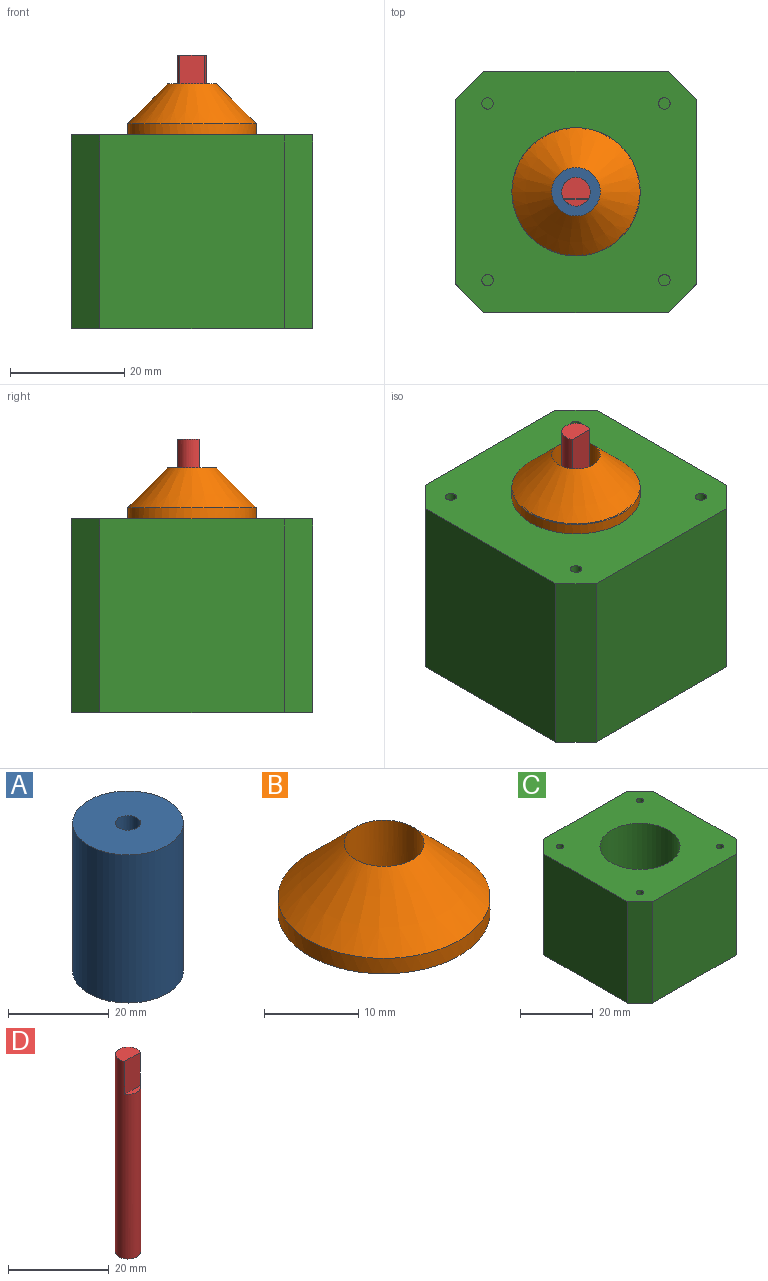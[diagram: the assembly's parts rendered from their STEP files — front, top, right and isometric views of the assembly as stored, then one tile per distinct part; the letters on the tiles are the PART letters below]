
ASSEMBLY  parts=4 mates=3
PART A: 4 faces, bbox 22x22x36 mm
  f0: cylinder r=2.5mm len=36mm, axis (0,0,-1), area 565.5mm2, adj f2,f3
  f1: cylinder r=11mm len=36mm, axis (0,0,-1), area 2488.1mm2, adj f2,f3
  f2: plane 22x22mm, normal (0,0,1), area 360.5mm2, adj f0,f1
  f3: plane 22x22mm, normal (0,0,-1), area 360.5mm2, adj f0,f1
PART B: 4 faces, bbox 22.5x22.5x9 mm
  f0: cylinder r=11.25mm len=22.5mm, axis (0,0,-1), area 141.4mm2, adj f2,f3
  f1: cylinder r=4.25mm len=9mm, axis (0,0,-1), area 240.3mm2, adj f2,f3
  f2: plane 22.5x22.5mm, normal (0,0,-1), area 340.9mm2, adj f0,f1
  f3: cone r=3.25mm half-angle=45deg, axis (0,0,-1), area 482.1mm2, adj f0,f1
PART C: 19 faces, bbox 42.3x42.3x34 mm
  f0: plane 34x32.3mm, normal (0,-1,0), area 1098.2mm2, adj f9,f10,f15,f16
  f1: plane 34x32.3mm, normal (1,0,0), area 1098.2mm2, adj f9,f10,f15,f18
  f2: plane 34x32.3mm, normal (0,1,0), area 1098.2mm2, adj f9,f10,f17,f18
  f3: cylinder r=1mm len=4.5mm, axis (0,0,-1), area 28.3mm2, adj f9,f11
  f4: cylinder r=1mm len=4.5mm, axis (0,0,-1), area 28.3mm2, adj f9,f12
  f5: cylinder r=1mm len=4.5mm, axis (0,0,-1), area 28.3mm2, adj f9,f13
  f6: cylinder r=1mm len=4.5mm, axis (0,0,-1), area 28.3mm2, adj f9,f14
  f7: cylinder r=11mm len=34mm, axis (0,0,-1), area 2349.9mm2, adj f9,f10
  f8: plane 34x32.3mm, normal (-1,0,0), area 1098.2mm2, adj f9,f10,f16,f17
  f9: plane 42.3x42.3mm, normal (0,0,1), area 1346.6mm2, adj f0,f1,f2,f3,f4,f5,f6,f7
  f10: plane 42.3x42.3mm, normal (0,0,-1), area 1359.2mm2, adj f0,f1,f2,f7,f8,f15,f16,f17
  f11: plane 2x2mm, normal (0,0,1), area 3.1mm2, adj f3
  f12: plane 2x2mm, normal (0,0,1), area 3.1mm2, adj f4
  f13: plane 2x2mm, normal (0,0,1), area 3.1mm2, adj f5
  f14: plane 2x2mm, normal (0,0,1), area 3.1mm2, adj f6
  f15: plane 34x5mm, normal (0.71,-0.71,0), area 240.4mm2, adj f0,f1,f9,f10
  f16: plane 34x5mm, normal (-0.71,-0.71,0), area 240.4mm2, adj f0,f8,f9,f10
  f17: plane 34x5mm, normal (-0.71,0.71,0), area 240.4mm2, adj f2,f8,f9,f10
  f18: plane 34x5mm, normal (0.71,0.71,0), area 240.4mm2, adj f1,f2,f9,f10
PART D: 5 faces, bbox 5x5x48 mm
  f0: plane 8x4.31mm, normal (0,-1,0), area 34.4mm2, adj f1,f2,f4
  f1: cylinder r=2.5mm len=48mm, axis (0,0,-1), area 712.5mm2, adj f0,f2,f3,f4
  f2: plane 5x3.77mm, normal (0,0,1), area 15.9mm2, adj f0,f1
  f3: plane 5x5mm, normal (0,0,-1), area 19.6mm2, adj f1
  f4: plane 4.31x1.23mm, normal (0,0,1), area 3.7mm2, adj f0,f1
PLACE A t=(17.86,0,23.04)mm
PLACE B rot(axis=(0,0,1),180deg) t=(-24.44,42.3,23.04)mm
PLACE C t=(17.86,0,23.04)mm
PLACE D t=(17.86,0,23.04)mm
MATE fastened A.f0 <-> D.f1  axis (0,0,-1) through (-3.29,21.15,23.04)mm
MATE fastened B.f0 <-> D.f1  axis (0,0,-1) through (-3.29,21.15,66.04)mm
MATE fastened A.f0 <-> C.f7  axis (0,0,-1) through (-3.29,21.15,40.04)mm
